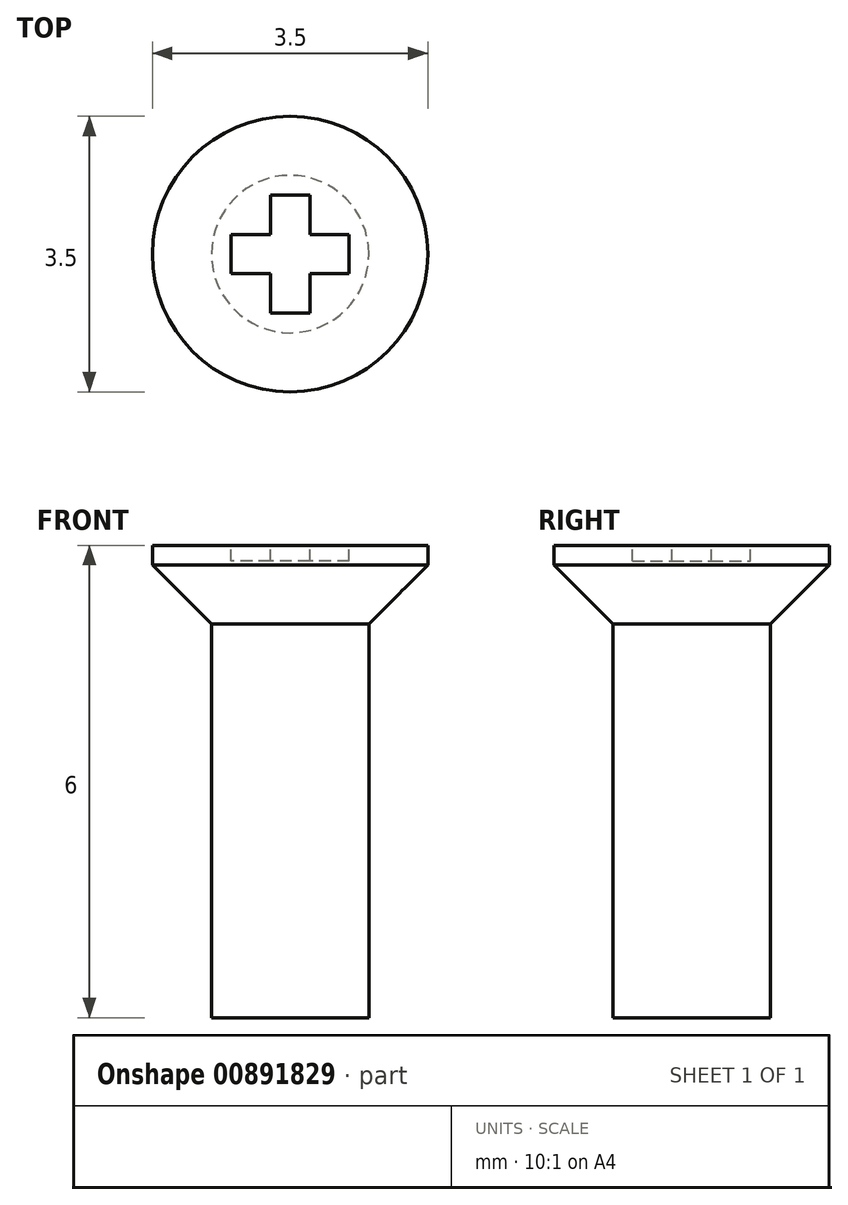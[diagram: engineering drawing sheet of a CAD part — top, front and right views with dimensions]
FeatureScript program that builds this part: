
annotation { "Feature Type Name" : "Feature", "Feature Type Description" : "" }
export const myFeature = defineFeature(function(context is Context, id is Id, definition is map)
    precondition{}
    {
        {
            var Q0;
            Q0=qCreatedBy(makeId("Top.planeOp"),FACE);
            var sketch = newSketch(context, id + "F0", { "sketchPlane" : qUnion([Q0])});
            skCircle(sketch, "E0", {"center": v(0, 0) * mm, "radius": 1.75 * mm});
            skSolve(sketch);
        }
        {
            var Q0;
            Q0=makeQuery(id+"F0.imprint","IMPRINT",FACE,{"disambiguationData":[TD([[makeQuery(id+"F0.imprint","IMPRINT",EDGE,{"derivedFrom":sQuery(id+"F0.wireOp",EDGE,"E0")}),1.0]])]});
            extrude(context, id + "F1", {"entities" : qUnion([Q0]), "depth" : 1 * mm, "offsetDistance" : 25 * mm});
        }
        {
            var Q0;
            Q0=makeQuery(id+"F1.opExtrude","CAP_EDGE",EDGE,{"disambiguationData":[OSD([sQuery(id+"F0.wireOp",EDGE,"E0")])],"isStart":true});
            chamfer(context, id + "F2", {"entities" : qUnion([Q0]), "width" : 0.75 * mm, "tangentPropagation" : true});
        }
        {
            var Q0;
            Q0=makeQuery(id+"F1.opExtrude","CAP_FACE",FACE,{"disambiguationData":[OSD([sQuery(id+"F0.wireOp",EDGE,"E0")])],"isStart":true});
            extrude(context, id + "F3", {"entities" : qUnion([Q0]), "operationType" : NewBodyOperationType.ADD, "depth" : 5 * mm, "offsetDistance" : 25 * mm});
        }
        {
            var Q0;
            Q0=makeQuery(id+"F1.opExtrude","CAP_FACE",FACE,{"disambiguationData":[OSD([sQuery(id+"F0.wireOp",EDGE,"E0")])],"isStart":false});
            var sketch = newSketch(context, id + "F4", { "sketchPlane" : qUnion([Q0])});
            skLineSegment(sketch, "E1.bottom", {"start": v(0.25, -0.75) * mm, "end": v(-0.25, -0.75) * mm});
            skLineSegment(sketch, "E1.top", {"start": v(0.25, 0.75) * mm, "end": v(-0.25, 0.75) * mm});
            skLineSegment(sketch, "E1.left", {"start": v(0.25, -0.75) * mm, "end": v(0.25, 0.75) * mm});
            skLineSegment(sketch, "E1.right", {"start": v(-0.25, -0.75) * mm, "end": v(-0.25, 0.75) * mm});
            skPoint(sketch, "E1.middle", {"position": v(0, 0) * mm});
            skLineSegment(sketch, "E2.bottom", {"start": v(0.75, -0.25) * mm, "end": v(-0.75, -0.25) * mm});
            skLineSegment(sketch, "E2.top", {"start": v(0.75, 0.25) * mm, "end": v(-0.75, 0.25) * mm});
            skLineSegment(sketch, "E2.left", {"start": v(0.75, -0.25) * mm, "end": v(0.75, 0.25) * mm});
            skLineSegment(sketch, "E2.right", {"start": v(-0.75, -0.25) * mm, "end": v(-0.75, 0.25) * mm});
            skSolve(sketch);
        }
        {
            var Q0;
            {var subQ0=sQuery(id+"F4.wireOp",EDGE,"E1.top");Q0=makeQuery(id+"F4.imprint","IMPRINT",FACE,{"disambiguationData":[TD([[makeQuery(id+"F4.imprint","IMPRINT",EDGE,{"derivedFrom":subQ0}),1.0]])]});}
            var Q1;
            {var subQ0=sQuery(id+"F4.wireOp",EDGE,"E2.bottom");var subQ1=sQuery(id+"F4.wireOp",EDGE,"E1.left");var subQ2=makeQuery(id+"F4.imprint","INTERSECT",VERTEX,{"derivedFrom":[subQ1,subQ0]});Q1=makeQuery(id+"F4.imprint","IMPRINT",FACE,{"disambiguationData":[TD([[makeQuery(id+"F4.imprint","IMPRINT",EDGE,{"disambiguationData":[TD([[subQ2,-1.0]])],"derivedFrom":subQ1}),1.0]])]});}
            var Q2;
            {var subQ5=sQuery(id+"F4.wireOp",EDGE,"E2.left");Q2=makeQuery(id+"F4.imprint","IMPRINT",FACE,{"disambiguationData":[TD([[makeQuery(id+"F4.imprint","IMPRINT",EDGE,{"derivedFrom":subQ5}),1.0]])]});}
            var Q3;
            {var subQ0=sQuery(id+"F4.wireOp",EDGE,"E1.bottom");Q3=makeQuery(id+"F4.imprint","IMPRINT",FACE,{"disambiguationData":[TD([[makeQuery(id+"F4.imprint","IMPRINT",EDGE,{"derivedFrom":subQ0}),-1.0]])]});}
            var Q4;
            {var subQ5=sQuery(id+"F4.wireOp",EDGE,"E2.right");Q4=makeQuery(id+"F4.imprint","IMPRINT",FACE,{"disambiguationData":[TD([[makeQuery(id+"F4.imprint","IMPRINT",EDGE,{"derivedFrom":subQ5}),-1.0]])]});}
            extrude(context, id + "F5", {"entities" : qUnion([Q0, Q1, Q2, Q3, Q4]), "operationType" : NewBodyOperationType.REMOVE, "oppositeDirection" : true, "depth" : 0.2 * mm, "offsetDistance" : 25 * mm});
        }
    });
